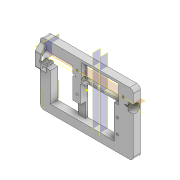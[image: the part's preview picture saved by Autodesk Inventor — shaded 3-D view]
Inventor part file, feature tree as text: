
AUTODESK INVENTOR PART (.ipt)
format: ipt  version: 2022 (Build 260153000, 153)  size: 439,808 bytes
history: native  units: mm
features: sketch x17, extrude x16, other x12, reference x8, plane x7, projected_geometry x7, fillet x3, chamfer x1, mirror x1
ambient origin geometry x8: Origin, YZ Plane, XZ Plane, XY Plane, X Axis, Y Axis, Z Axis, Center Point
bodies: Solid1 (feature_tree)
feature tree (72):
  extrude  "Extrusion1"  Depth=10.0mm
  fillet  "Fillet1"  Radius=10.0mm
  extrude  "Extrusion2"  Depth=51.0mm
  extrude  "Extrusion3"  Depth=20.0mm
  plane  "Work Plane1"
  plane  "Work Plane2"
  chamfer  "Chamfer1"  [1 undecoded]
  plane  "Work Plane3"
  extrude  "Extrusion12"  Depth=10.0mm
  extrude  "Extrusion13"  Depth=12.0mm
  mirror  "Mirror1"
  plane  "Work Plane4"
  plane  "Work Plane5"
  plane  "Arbeitsebene7"
  extrude  "Extrusion27"  Depth=7.0mm
  extrude  "Extrusion28"  Depth=0.5mm TaperAngle=0.0deg
  extrude  "Extrusion29"  Depth=0.5mm
  fillet  "Rundung6"  Radius=1.0mm
  extrude  "Extrusion37"  TaperAngle=45.0deg  [1 undecoded]
  extrude  "Extrusion38"  Depth=10.0mm
  fillet  "Rundung7"  [1 undecoded]
  extrude  "Extrusion39"  Depth=10.0mm TaperAngle=0.0deg
  other  "Arbeitsachse1"
  sketch  "Skizze44"  dims[d145=8.0mm d146=0.0mm d147=0.5mm d148=1.0mm d149=0.0mm]
  extrude  "Extrusion41"  TaperAngle=0.0deg  [1 undecoded]
  extrude  "Extrusion42"  Depth=2.0mm TaperAngle=0.0deg
  extrude  "Extrusion43"  Depth=2.5mm
  extrude  "Extrusion44"  Depth=0.5mm
  sketch  "Skizze49"  dims[d195=20.0mm d196=2.0mm d197=0.0mm d199=14.0mm d201=0.5mm d203=0.5mm d204=1.0mm d205=3.0mm d206=2.8mm d207=2.8mm d208=2.8mm d209=2.8mm d210=2.8mm d211=0.0mm d212=0.0mm d213=3.0mm d214=0.0mm d215=6.0mm d216=2.0mm d217=3.0mm d218=0.0mm d219=2.5mm d220=0.0mm]
  plane  "Arbeitsebene10"
  extrude  "Extrusion45"  Depth=0.5mm
  sketch  "Sketch1"  dims[d0=127.8mm d1=85.5mm d2=10.0mm d3=0.0mm]
  sketch  "Sketch2"  dims[d4=4.0mm d5=51.0mm]
  projected_geometry  "Projected Loop1"
  sketch  "Sketch3"  dims[d6=25.0mm d7=20.0mm]
  projected_geometry  "Projected Loop2"
  sketch  "Sketch12"  dims[d8=13.0mm]
  reference  "Reference4"
  sketch  "Sketch13"  dims[d9=6.0mm]
  sketch  "Skizze28"  dims[d10=0.0mm]
  sketch  "Skizze29"  dims[d11=1.5mm d12=0.0mm d13=0.0mm]
  reference  "Referenz13"
  sketch  "Skizze30"  dims[d14=4.0mm d15=2.0mm d16=45.0deg d38=10.0mm]
  reference  "Referenz14"
  sketch  "Skizze40"  dims[d61=30.0mm d62=-0.523599mm d63=12.0mm]
  projected_geometry  "Projizierte Kontur18"
  sketch  "Skizze41"  dims[d64=7.0mm d65=0.0mm d100=7.0mm]
  projected_geometry  "Projizierte Kontur19"
  sketch  "Skizze42"  dims[d142=0.5mm d143=40.0mm d144=0.0mm]
  reference  "Referenz22"
  reference  "Referenz23"
  reference  "Referenz24"
  reference  "Referenz25"
  sketch  "Skizze45"  dims[d150=2.0mm d151=45.0deg]
  sketch  "Skizze46"  dims[d152=45.0deg d178=10.0mm d179=0.0mm d180=0.0mm]
  projected_geometry  "Projizierte Kontur20"
  sketch  "Skizze47"  dims[d181=14.0mm d182=10.0mm d183=0.0mm]
  projected_geometry  "Projizierte Kontur21"
  sketch  "Skizze48"  dims[d184=5.0mm d187=0.0mm d188=0.0mm]
  projected_geometry  "Projizierte Kontur22"
  reference  "Referenz29"
  other  "<userpath>\Documents\GitHub\Guinardia\INVENTOR\Assembly_Guinardia_V1.iam"
  other  "Assembly_Guinardia_V1.iam"
  other  "00_PipetteTip200ul-1:2"
  other  "00_NEMA8:1"
  other  "Assembly_Guinardia_V2.iam"
  other  "Assemlby_Scanner_v1:1"
  other  "30_Scanlens_Laseradaper_v1:1"
  other  "30_Scanlens_Laseradaper_lid_v1:1"
  other  "00_Coverglass_50x24mm:2"
  other  "<userpath>\Documents\Inventor\Guinardia\INVENTOR\Assembly_Guinardia_V0.iam"
  other  "Assembly_Guinardia_V0.iam"
note: 4 required parameter values undecoded (feature->parameter linkage not recoverable at this tier; creation-order binding heuristic only, values carry confidence <= 0.55)
